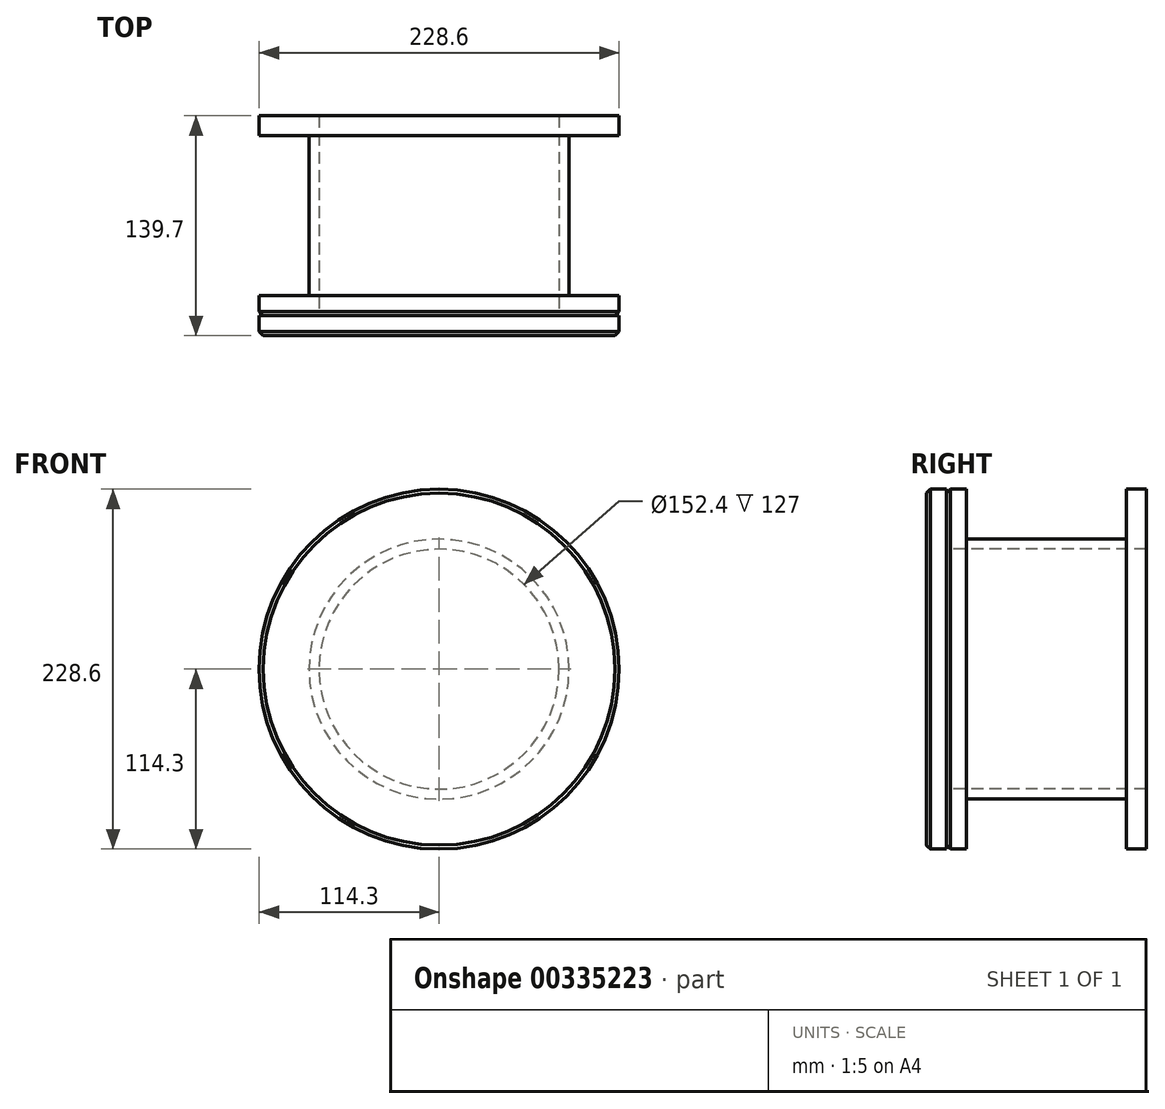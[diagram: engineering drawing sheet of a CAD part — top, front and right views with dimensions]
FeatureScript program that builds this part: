
annotation { "Feature Type Name" : "Feature", "Feature Type Description" : "" }
export const myFeature = defineFeature(function(context is Context, id is Id, definition is map)
    precondition{}
    {
        {
            var Q0;
            Q0=qCreatedBy(makeId("Right.planeOp"),FACE);
            var sketch = newSketch(context, id + "F0", { "sketchPlane" : qUnion([Q0])});
            skLineSegment(sketch, "E0", {"start": v(-372.41, 0) * mm, "end": v(512.39, 0) * mm, "construction": true});
            skLineSegment(sketch, "E1", {"start": v(0, 114.3) * mm, "end": v(-12.7, 114.3) * mm});
            skLineSegment(sketch, "E2", {"start": v(-12.7, 114.3) * mm, "end": v(-12.7, 82.55) * mm});
            skLineSegment(sketch, "E3", {"start": v(-12.7, 82.55) * mm, "end": v(-114.3, 82.55) * mm});
            skLineSegment(sketch, "E4", {"start": v(-114.3, 82.55) * mm, "end": v(-114.3, 114.3) * mm});
            skLineSegment(sketch, "E5", {"start": v(-114.3, 114.3) * mm, "end": v(-127, 114.3) * mm});
            skLineSegment(sketch, "E6", {"start": v(-127, 76.2) * mm, "end": v(0, 76.2) * mm});
            skLineSegment(sketch, "E7", {"start": v(-127, 114.3) * mm, "end": v(-127, 76.2) * mm});
            skLineSegment(sketch, "E8", {"start": v(0, 114.3) * mm, "end": v(0, 76.2) * mm});
            skSolve(sketch);
        }
        {
            var Q0;
            Q0=makeQuery(id+"F0.imprint","IMPRINT",FACE,{"disambiguationData":[TD([[makeQuery(id+"F0.imprint","IMPRINT",EDGE,{"derivedFrom":sQuery(id+"F0.wireOp",EDGE,"E1")}),1.0]])]});
            var Q1;
            Q1=sQuery(id+"F0.wireOp",EDGE,"E0");
            revolve(context, id + "F1", {"entities" : qUnion([Q0]), "axis" : qUnion([Q1]), "revolveType" : RevolveType.FULL});
        }
        {
            var Q0;
            Q0=makeQuery(id+"F1.opRevolve","SWEPT_FACE",FACE,{"disambiguationData":[OSD([sQuery(id+"F0.wireOp",EDGE,"E7")])]});
            cPlane(context, id + "F2", {"entities" : qUnion([Q0]), "cplaneType" : CPlaneType.OFFSET, "offset" : 0 * mm, "width" : 152.4 * mm, "height" : 152.4 * mm});
        }
        {
            var Q0;
            Q0=qCreatedBy(id+"F2.planeOp",FACE);
            var sketch = newSketch(context, id + "F3", { "sketchPlane" : qUnion([Q0])});
            skCircle(sketch, "E9", {"center": v(0, 0) * mm, "radius": 114.3 * mm});
            skSolve(sketch);
        }
        {
            var Q0;
            Q0=makeQuery(id+"F3.imprint","IMPRINT",FACE,{"disambiguationData":[TD([[makeQuery(id+"F3.imprint","IMPRINT",EDGE,{"derivedFrom":sQuery(id+"F3.wireOp",EDGE,"E9")}),1.0]])]});
            extrude(context, id + "F4", {"entities" : qUnion([Q0]), "depth" : 12.7 * mm});
        }
        {
            var Q0;
            Q0=makeQuery(id+"F1.opRevolve","SWEPT_EDGE",EDGE,{"disambiguationData":[OSD([sQuery(id+"F0.wireOp",EDGE,"E5"),sQuery(id+"F0.wireOp",EDGE,"E7")])]});
            var Q1;
            Q1=makeQuery(id+"F4.opExtrude","CAP_EDGE",EDGE,{"disambiguationData":[OSD([sQuery(id+"F3.wireOp",EDGE,"E9")])],"isStart":false});
            chamfer(context, id + "F5", {"entities" : qUnion([Q0, Q1]), "width" : 2.54 * mm, "tangentPropagation" : true});
        }
    });
